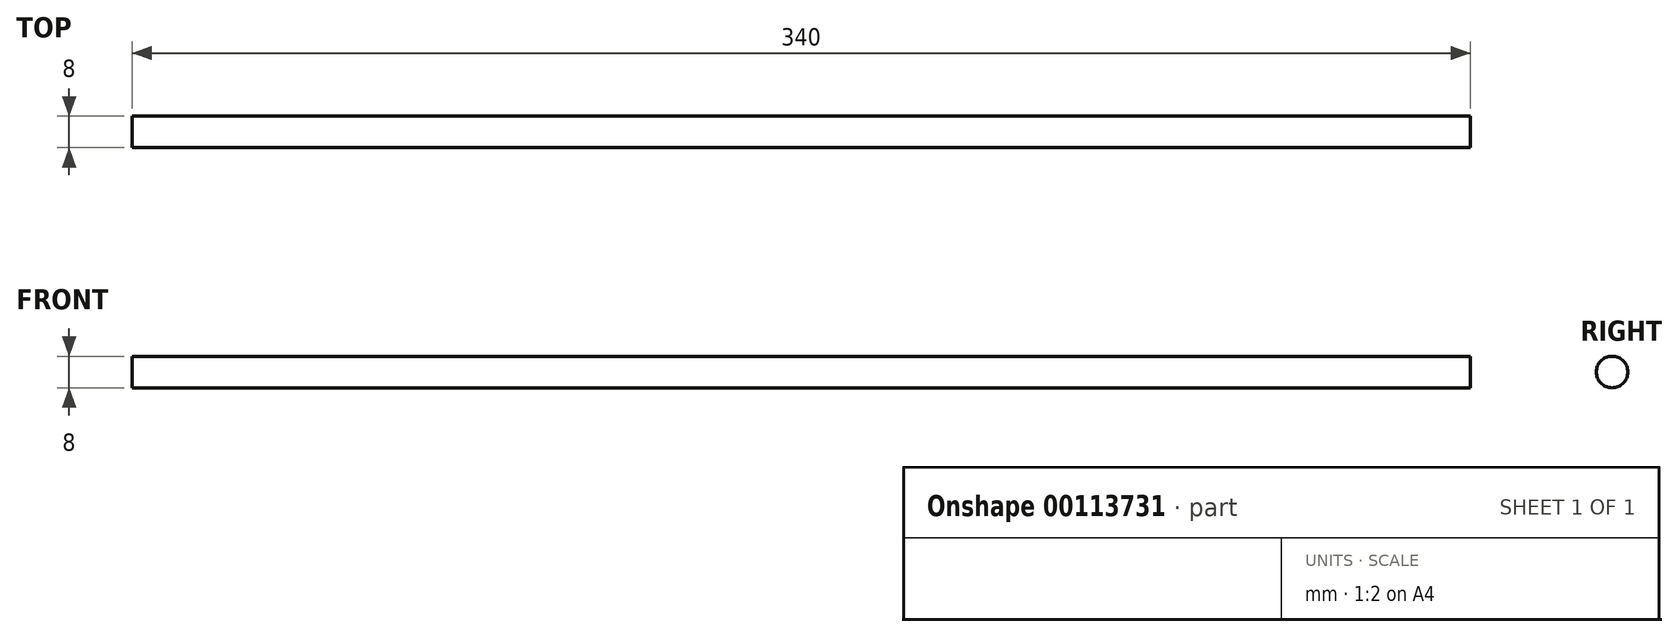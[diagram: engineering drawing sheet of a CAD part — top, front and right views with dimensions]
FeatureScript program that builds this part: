
annotation { "Feature Type Name" : "Feature", "Feature Type Description" : "" }
export const myFeature = defineFeature(function(context is Context, id is Id, definition is map)
    precondition{}
    {
        {
            var Q0;
            Q0=qCreatedBy(makeId("Right.planeOp"),FACE);
            var sketch = newSketch(context, id + "F0", { "sketchPlane" : qUnion([Q0])});
            skCircle(sketch, "E0", {"center": v(0, 0) * mm, "radius": 4 * mm});
            skSolve(sketch);
        }
        {
            var Q0;
            Q0=makeQuery(id+"F0.imprint","IMPRINT",FACE,{"disambiguationData":[TD([[makeQuery(id+"F0.imprint","IMPRINT",EDGE,{"derivedFrom":sQuery(id+"F0.wireOp",EDGE,"E0")}),1.0]])]});
            extrude(context, id + "F1", {"entities" : qUnion([Q0]), "depth" : 340 * mm});
        }
    });
